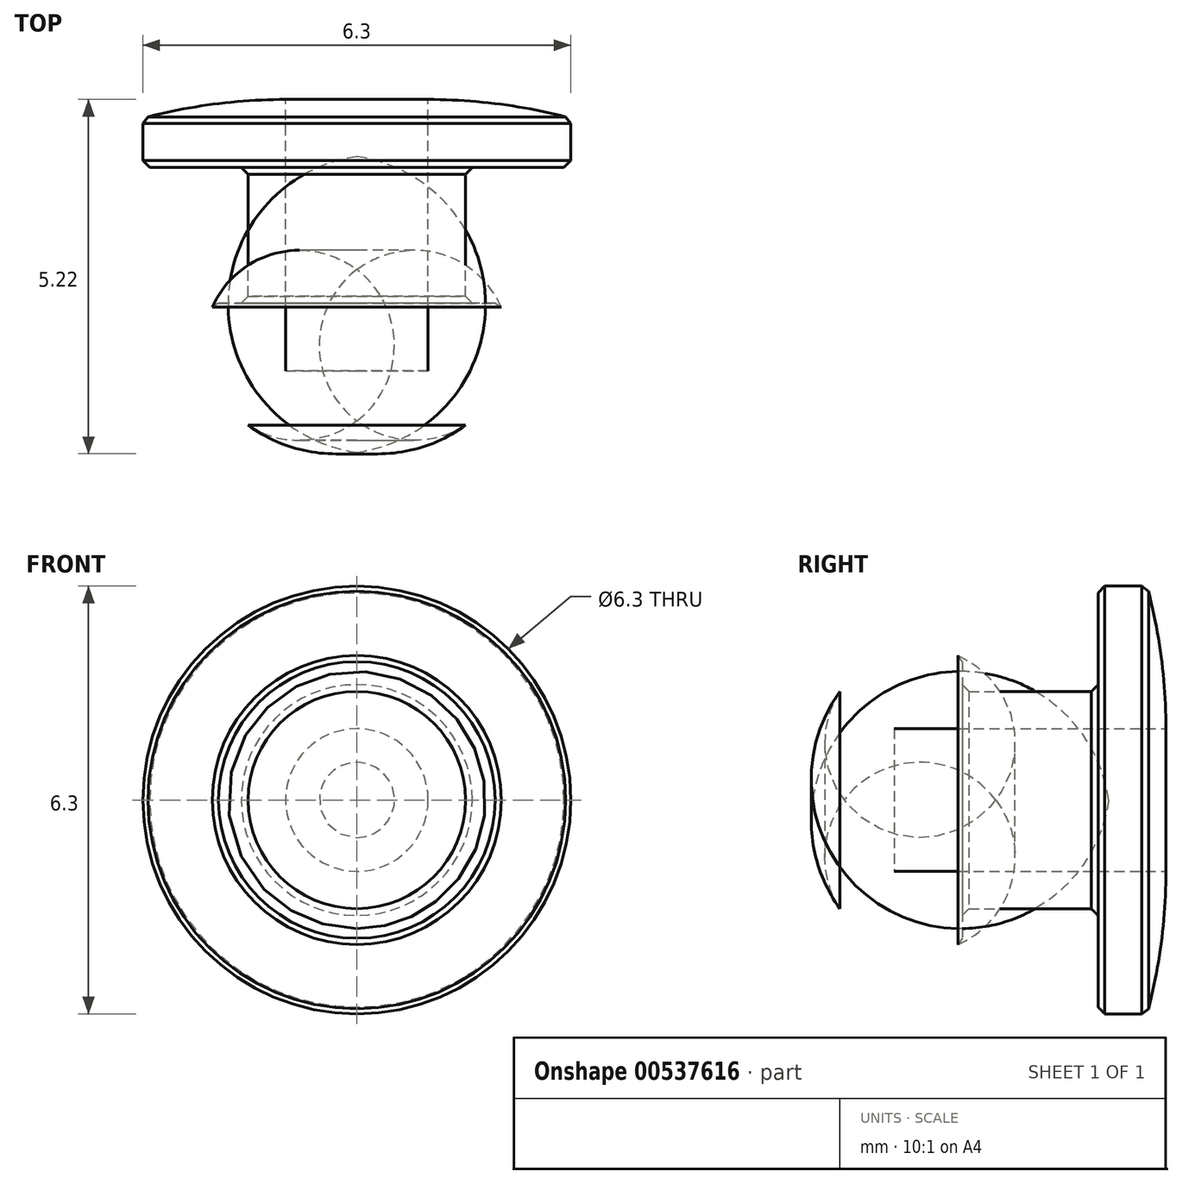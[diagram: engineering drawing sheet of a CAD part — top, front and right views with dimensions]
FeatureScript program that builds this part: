
annotation { "Feature Type Name" : "Feature", "Feature Type Description" : "" }
export const myFeature = defineFeature(function(context is Context, id is Id, definition is map)
    precondition{}
    {
        {
            var Q0;
            Q0=qCreatedBy(makeId("Right.planeOp"),FACE);
            var sketch = newSketch(context, id + "F0", { "sketchPlane" : qUnion([Q0])});
            skLineSegment(sketch, "E0", {"start": v(0, 1.05) * mm, "end": v(3, 1.05) * mm});
            skLineSegment(sketch, "E1", {"start": v(2.72, 3.15) * mm, "end": v(2, 3.15) * mm});
            skLineSegment(sketch, "E2", {"start": v(2, 3.15) * mm, "end": v(2, 1.6) * mm});
            skLineSegment(sketch, "E3", {"start": v(2, 1.6) * mm, "end": v(0, 1.6) * mm});
            skLineSegment(sketch, "E4", {"start": v(0, 1.6) * mm, "end": v(0, 2.1) * mm});
            skArc(sketch, "E5", {"start": v(0, 2.1) * mm, "mid": v(-1, 2.2) * mm, "end": v(-1.8, 1.6) * mm});
            skArc(sketch, "E6", {"start": v(-1.8, 1.6) * mm, "mid": v(-2.16, 0.84) * mm, "end": v(-2.2, 0) * mm});
            skLineSegment(sketch, "E7", {"start": v(0, 1.05) * mm, "end": v(-1, 1.05) * mm});
            skLineSegment(sketch, "E8", {"start": v(-1, 1.05) * mm, "end": v(-1, 0) * mm});
            skLineSegment(sketch, "E9", {"start": v(-1, 0) * mm, "end": v(-2.2, 0) * mm});
            skArc(sketch, "E10", {"start": v(3, 1.05) * mm, "mid": v(2.93, 2.1) * mm, "end": v(2.72, 3.15) * mm});
            skPoint(sketch, "E11.end.orphan", {"position": v(3, 3.15) * mm});
            skSolve(sketch);
        }
        {
            var Q0;
            Q0=makeQuery(id+"F0.imprint","IMPRINT",FACE,{"disambiguationData":[TD([[makeQuery(id+"F0.imprint","IMPRINT",EDGE,{"derivedFrom":sQuery(id+"F0.wireOp",EDGE,"E0")}),1.0]])]});
            var Q1;
            Q1=sQuery(id+"F0.wireOp",EDGE,"E9");
            revolve(context, id + "F1", {"entities" : qUnion([Q0]), "axis" : qUnion([Q1]), "revolveType" : RevolveType.FULL});
        }
        {
            var Q0;
            Q0=makeQuery(id+"F1.opRevolve","SWEPT_EDGE",EDGE,{"disambiguationData":[OSD([sQuery(id+"F0.wireOp",EDGE,"E1"),sQuery(id+"F0.wireOp",EDGE,"E2")])]});
            var Q1;
            Q1=makeQuery(id+"F1.opRevolve","SWEPT_EDGE",EDGE,{"disambiguationData":[OSD([sQuery(id+"F0.wireOp",EDGE,"E4"),sQuery(id+"F0.wireOp",EDGE,"E5")])]});
            var Q2;
            Q2=makeQuery(id+"F1.opRevolve","SWEPT_EDGE",EDGE,{"disambiguationData":[OSD([sQuery(id+"F0.wireOp",EDGE,"E2"),sQuery(id+"F0.wireOp",EDGE,"E3")])]});
            var Q3;
            Q3=makeQuery(id+"F1.opRevolve","SWEPT_EDGE",EDGE,{"disambiguationData":[OSD([sQuery(id+"F0.wireOp",EDGE,"E3"),sQuery(id+"F0.wireOp",EDGE,"E4")])]});
            var Q4;
            Q4=makeQuery(id+"F1.opRevolve","SWEPT_EDGE",EDGE,{"disambiguationData":[OSD([sQuery(id+"F0.wireOp",EDGE,"E1"),sQuery(id+"F0.wireOp",EDGE,"E10")])]});
            chamfer(context, id + "F2", {"entities" : qUnion([Q0, Q1, Q2, Q3, Q4]), "width" : 0.1 * mm, "tangentPropagation" : true});
        }
    });
